# Revit family: CADS_AIRFLOWdev_Speed_Switches
name_source: partatom
category: Electrical Fixtures
revit_build: Autodesk Revit 2015 (Build: 20160512_1515(x64)
units: mm (PartAtom-declared; Revit-internal decimal feet)

## types (1)
- 1 amp electronic illuminated stepless speed controller reversible
    AssetType = Fixed
    Body = CADS_AirFlow_White
    Box = 77 mm  [stored 0.252625 ft]
    Box_H = 70 mm  [stored 0.229659 ft]
    CADS_Index = 0
    CEApproval = Yes
    Color = White
    Constituents = White
    Default Elevation = 1219 mm
    Description = 1 amp electronic illuminated stepless speed controller reversible
    Dial_Depth = 10 mm  [stored 0.0328084 ft]
    Dial_Dia = 40 mm  [stored 0.131234 ft]
    Dial_Offset = 0 mm  [stored 0 ft]
    DurationUnit = Years
    Exclusions = Incorrect Use / Incorrect Installation / Installed by a non-accredited electrician. Customer abuse.
    Finish = White
    GlobalTradeItemNumber = 5019009307787
    GrossWeight = 0.30 kg
    HasLock = No
    HasProtectiveEarth = No
    ISO140001 = Yes
    ISO90001 = Yes
    IsExtendedWarranty = No
    IsIlluminated = Yes
    Manufacturer = Airflow Developments Ltd
    ManufacturerAddress = Aidelle House
Lancaster Road
Cressex Business Park
High Wycombe
Bucks
HP123QP
    ManufacturerTelephone = 01494 525252
    ManufacturerWebsite = www.airflow.com
    Material = Plastic
    ModelLabel = 1 amp electronic illuminated stepless speed controller reversible
    ModelReference = 9041566
    NBSCode = 90-60-25/330 Dimmer switches and controls;
    NominalFrequencyRange = 50/60
    NominalHeight = 77 mm  [stored 0.252625 ft]
    NominalLength = 70 mm  [stored 0.229659 ft]
    NominalWidth = 77 mm  [stored 0.252625 ft]
    NumberOfGangs = 1
    NumberOfPoles = 1
    PointOfContact = Airflow Developments Ltd
    ProductionYear = 2017
    Quantity = 1
    RatedCurrent = 1 A
    RatedVoltage = 240 V
    ReplacementCost = 119.352
    ServiceLifeDuration = 10
    ServiceLifeType = ExpectedServiceLife
    SetPoint = Variable
    Shape = Rectangular
    ShippingWeight = 0.40 kg
    Size = 77x70x77
    SupplyPhase = 1
    SwitchFunction = Rotary
    Uniclass2015 = Pr_65_72_97_22
    WarrantyContent = See Airflow Developments Ltd warranty terms.
    WarrantyGuarantor = Airflow Developments Ltd

note: [stored X ft] marks values corroborated as IEEE doubles in the binary element streams (Revit-internal decimal feet)

## geometry (parser evidence)
native form markers: Blend x2, Sweep x6
no freeform markers — native parametric forms only
